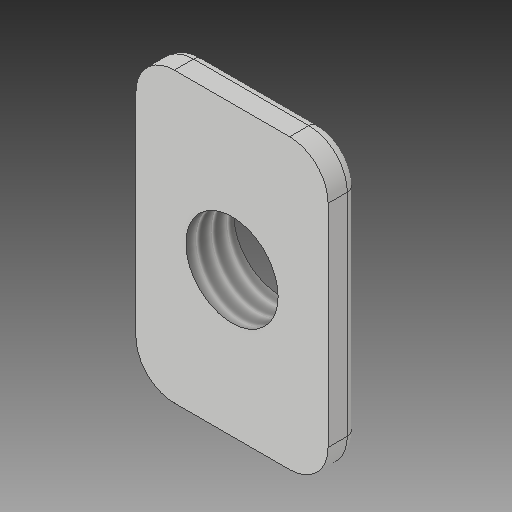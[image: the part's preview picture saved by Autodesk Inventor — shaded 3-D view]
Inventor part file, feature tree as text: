
AUTODESK INVENTOR PART (.ipt)
format: ipt  version: 2017 (Build 210142000, 142)  size: 144,384 bytes
history: native  units: mm
features: other x3, sketch x2
ambient origin geometry x8: Origin, YZ Plane, XZ Plane, XY Plane, X Axis, Y Axis, Z Axis, Center Point
bodies: Solid1 (feature_tree)
feature tree (5):
  other  "M5 Tee Nut.ipt"
  other  "Solid1::M5 Tee Nut.ipt"
  other  "TaggingFeature1"
  sketch  "Sketch1"  dims[d0=10.0mm]
  sketch  "Sketch2"
